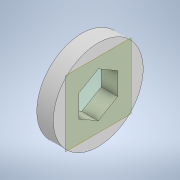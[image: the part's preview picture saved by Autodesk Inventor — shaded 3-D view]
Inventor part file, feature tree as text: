
AUTODESK INVENTOR PART (.ipt)
format: ipt  version: 2021 (Build 250183000, 183)  size: 102,912 bytes
history: native  units: mm
features: plane x1, extrude x1, sketch x1, projected_geometry x1
ambient origin geometry x8: Origin, YZ Plane, XZ Plane, XY Plane, X Axis, Y Axis, Z Axis, Center Point
bodies: Body1 (feature_tree)
feature tree (4):
  plane  "Work Plane1"
  extrude  "Extrusion1"  [1 undecoded]
  sketch  "Sketch1"  dims[d1=5.5mm d2=0.0mm]
  projected_geometry  "Projected Loop1"
note: 1 required parameter value undecoded (feature->parameter linkage not recoverable at this tier; creation-order binding heuristic only, values carry confidence <= 0.55)
